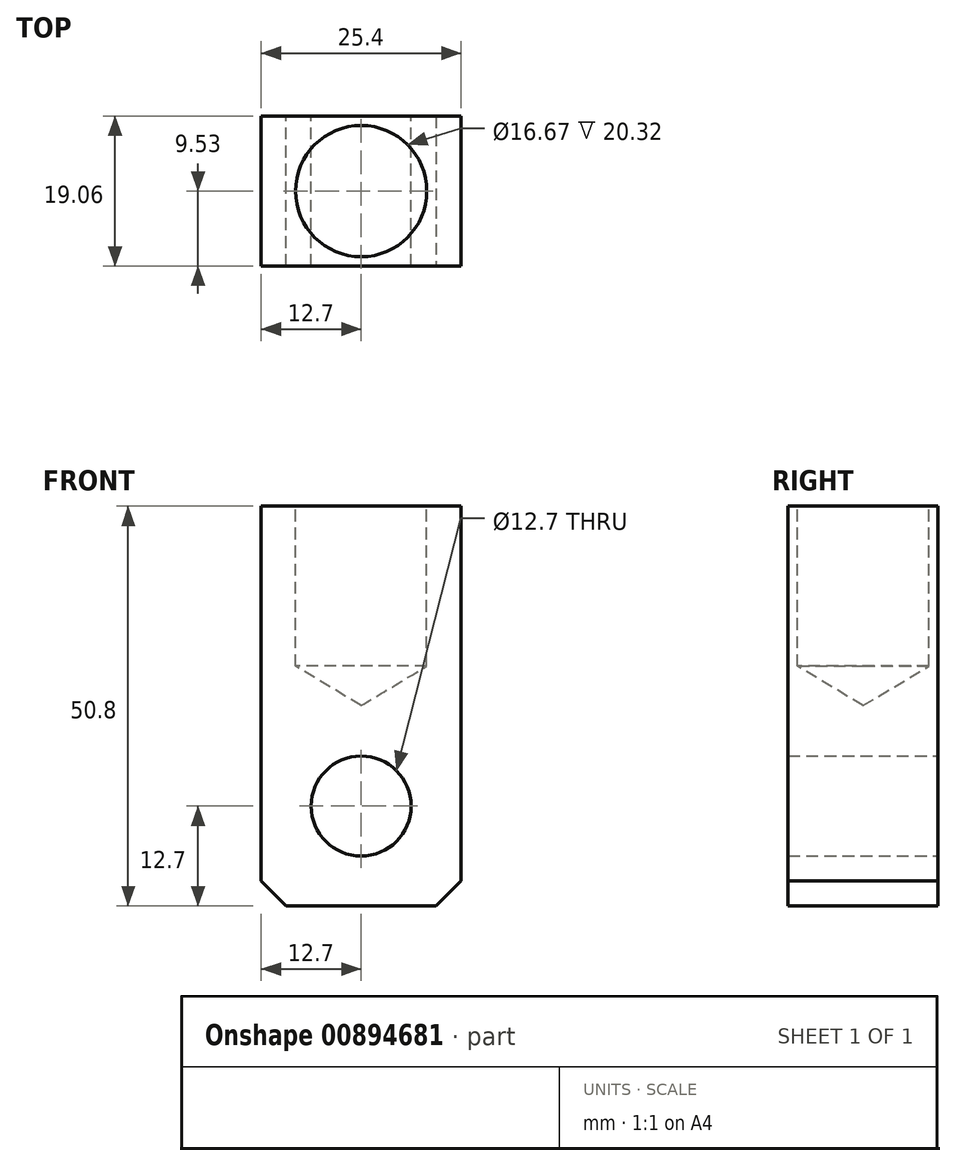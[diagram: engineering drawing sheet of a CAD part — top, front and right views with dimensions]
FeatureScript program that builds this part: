
annotation { "Feature Type Name" : "Feature", "Feature Type Description" : "" }
export const myFeature = defineFeature(function(context is Context, id is Id, definition is map)
    precondition{}
    {
        {
            var Q0;
            Q0=qCreatedBy(makeId("Front.planeOp"),FACE);
            var sketch = newSketch(context, id + "F0", { "sketchPlane" : qUnion([Q0])});
            skLineSegment(sketch, "E0.bottom", {"start": v(12.7, 25.4) * mm, "end": v(-12.7, 25.4) * mm});
            skLineSegment(sketch, "E0.top", {"start": v(12.7, -25.4) * mm, "end": v(-12.7, -25.4) * mm});
            skLineSegment(sketch, "E0.left", {"start": v(12.7, 25.4) * mm, "end": v(12.7, -25.4) * mm});
            skLineSegment(sketch, "E0.right", {"start": v(-12.7, 25.4) * mm, "end": v(-12.7, -25.4) * mm});
            skPoint(sketch, "E0.middle", {"position": v(0, 0) * mm});
            skCircle(sketch, "E1", {"center": v(0, -12.7) * mm, "radius": 6.35 * mm});
            skSolve(sketch);
        }
        {
            var Q0;
            Q0 = qSketchRegion(id + "F0", true);
            extrude(context, id + "F1", {"entities" : qUnion([Q0]), "endBound" : BoundingType.SYMMETRIC, "depth" : 19.05 * mm, "offsetDistance" : 25.4 * mm});
        }
        {
            var Q0;
            Q0=makeQuery(id+"F1.opExtrude","SWEPT_EDGE",EDGE,{"disambiguationData":[OSD([sQuery(id+"F0.wireOp",EDGE,"E0.top"),sQuery(id+"F0.wireOp",EDGE,"E0.left")])]});
            var Q1;
            Q1=makeQuery(id+"F1.opExtrude","SWEPT_EDGE",EDGE,{"disambiguationData":[OSD([sQuery(id+"F0.wireOp",EDGE,"E0.top"),sQuery(id+"F0.wireOp",EDGE,"E0.right")])]});
            chamfer(context, id + "F2", {"entities" : qUnion([Q0, Q1]), "width" : 3.17 * mm, "tangentPropagation" : true});
        }
        {
            var Q0;
            Q0=makeQuery(id+"F1.opExtrude","SWEPT_FACE",FACE,{"disambiguationData":[OSD([sQuery(id+"F0.wireOp",EDGE,"E0.bottom")])]});
            var sketch = newSketch(context, id + "F3", { "sketchPlane" : qUnion([Q0])});
            skPoint(sketch, "E2", {"position": v(0, 0) * mm});
            skSolve(sketch);
        }
        {
            var Q0;
            Q0=sQuery(id+"F3.wireOp",VERTEX,"E2");
            var Q1;
            Q1=makeQuery(id+"F1.opExtrude","SWEPT_BODY",BODY,{"disambiguationData":[OSD([sQuery(id+"F0.wireOp",EDGE,"E0.bottom"),sQuery(id+"F0.wireOp",EDGE,"E0.top"),sQuery(id+"F0.wireOp",EDGE,"E0.left"),sQuery(id+"F0.wireOp",EDGE,"E0.right"),sQuery(id+"F0.wireOp",EDGE,"E1")])]});
            hole(context, id + "F4", {"style" : HoleStyle.SIMPLE, "endStyle" : HoleEndStyle.BLIND, "standardTappedOrClearance" : lookupTablePath({ "standard" : "ANSI", "engagement" : "75%", "pitch" : "10 tpi", "size" : "3/4", "type" : "Tapped" }), "standardBlindInLast" : lookupTablePath({ "standard" : "ANSI", "engagement" : "75%", "pitch" : "10 tpi", "size" : "3/4", "type" : "Tapped" }), "holeDiameter" : 16.67 * mm, "majorDiameter" : 19.05 * mm, "showTappedDepth" : true, "holeDepth" : 20.32 * mm, "isTappedThrough" : true, "tappedDepth" : 12.7 * mm, "tapClearance" : 3, "startFromSketch" : true, "locations" : qUnion([Q0]), "scope" : qUnion([Q1])});
        }
    });
